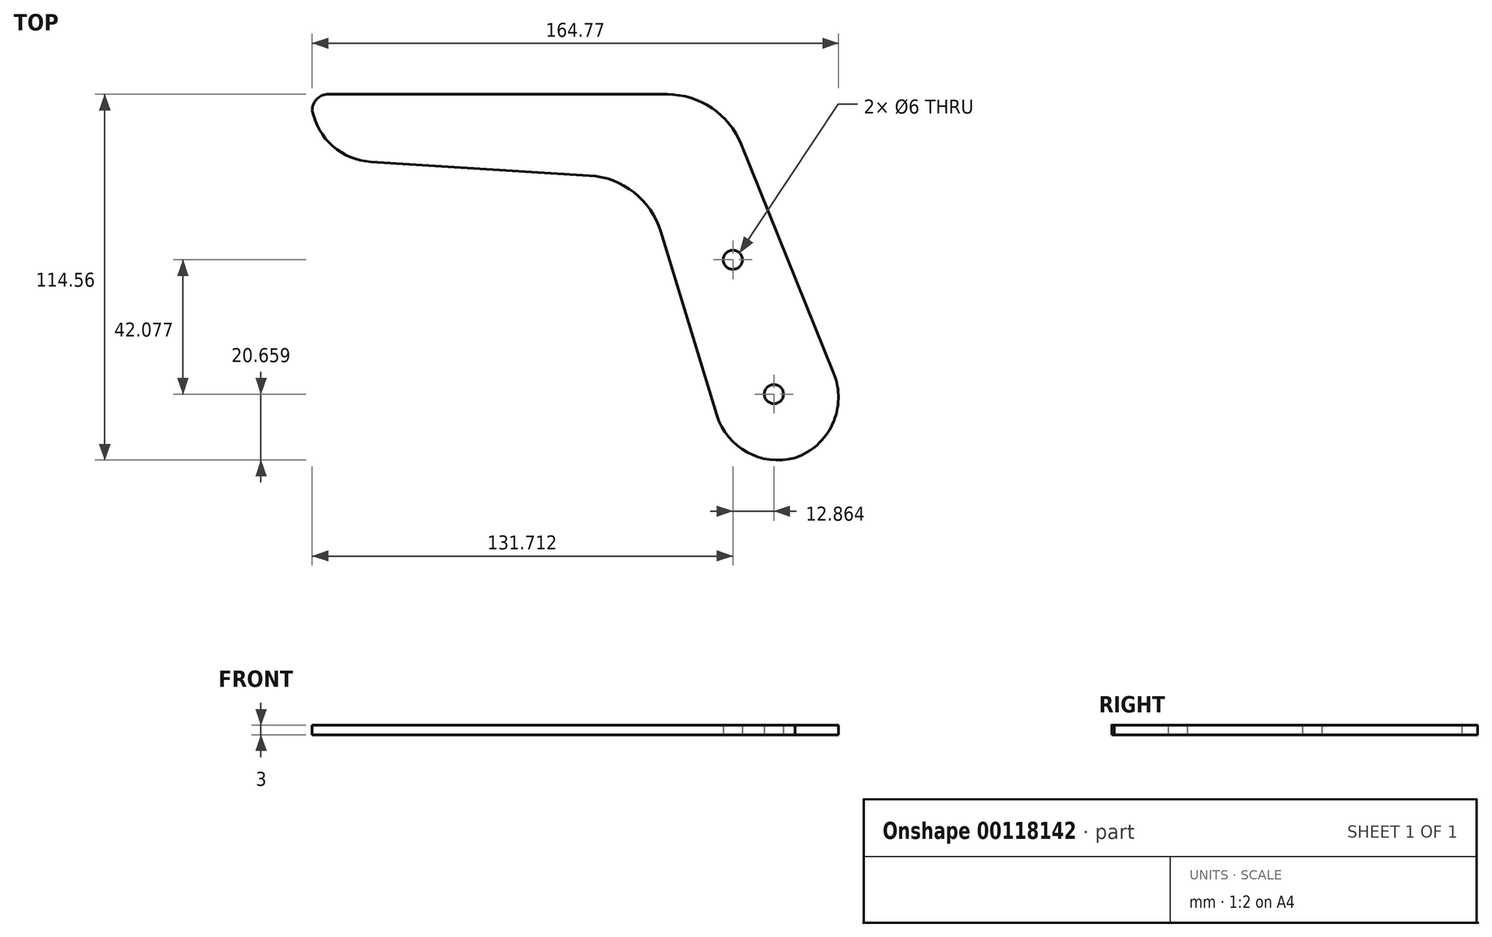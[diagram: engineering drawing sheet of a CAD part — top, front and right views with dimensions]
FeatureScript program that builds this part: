
annotation { "Feature Type Name" : "Feature", "Feature Type Description" : "" }
export const myFeature = defineFeature(function(context is Context, id is Id, definition is map)
    precondition{}
    {
        {
            var Q0;
            Q0=qCreatedBy(makeId("Top.planeOp"),FACE);
            var sketch = newSketch(context, id + "F0", { "sketchPlane" : qUnion([Q0])});
            skLineSegment(sketch, "E0", {"start": v(0, 0) * mm, "end": v(-128, 0) * mm});
            skLineSegment(sketch, "E1", {"start": v(-128, 0) * mm, "end": v(-128, -20) * mm});
            skLineSegment(sketch, "E2", {"start": v(0, 0) * mm, "end": v(0, -28) * mm, "construction": true});
            skLineSegment(sketch, "E3", {"start": v(-128, -20) * mm, "end": v(-23.9, -26.5) * mm});
            skLineSegment(sketch, "E4", {"start": v(0, 0) * mm, "end": v(43.49, -107.63) * mm});
            skPoint(sketch, "E5", {"position": v(-32, 0) * mm});
            skLineSegment(sketch, "E6", {"start": v(-32, 0) * mm, "end": v(-23.9, -26.5) * mm, "construction": true});
            skLineSegment(sketch, "E7", {"start": v(-23.9, -26.5) * mm, "end": v(0, -28) * mm, "construction": true});
            skLineSegment(sketch, "E8", {"start": v(-23.9, -26.5) * mm, "end": v(4.55, -119.54) * mm});
            skLineSegment(sketch, "E9", {"start": v(4.55, -119.54) * mm, "end": v(43.49, -107.63) * mm});
            skLineSegment(sketch, "E10.0", {"start": v(-12.13, 0) * mm, "end": v(22.72, -113.98) * mm, "construction": true});
            skPoint(sketch, "E11", {"position": v(16.58, -93.9) * mm});
            skPoint(sketch, "E12", {"position": v(3.71, -51.82) * mm});
            skCircle(sketch, "E13", {"center": v(3.71, -51.82) * mm, "radius": 3 * mm});
            skCircle(sketch, "E14", {"center": v(16.58, -93.9) * mm, "radius": 3 * mm});
            skSolve(sketch);
        }
        {
            var Q0;
            Q0=makeQuery(id+"F0.imprint","IMPRINT",FACE,{"disambiguationData":[TD([[makeQuery(id+"F0.imprint","IMPRINT",EDGE,{"derivedFrom":sQuery(id+"F0.wireOp",EDGE,"E0")}),1.0]])]});
            extrude(context, id + "F1", {"entities" : qUnion([Q0]), "depth" : 3 * mm});
        }
        {
            var Q0;
            Q0=makeQuery(id+"F1.opExtrude","SWEPT_EDGE",EDGE,{"disambiguationData":[OSD([sQuery(id+"F0.wireOp",EDGE,"E0"),sQuery(id+"F0.wireOp",EDGE,"E1")])]});
            fillet(context, id + "F2", {"entities" : qUnion([Q0]), "radius" : 5 * mm, "tangentPropagation" : true, "allowEdgeOverflow" : false});
        }
        {
            var Q0;
            Q0=makeQuery(id+"F1.opExtrude","SWEPT_EDGE",EDGE,{"disambiguationData":[OSD([sQuery(id+"F0.wireOp",EDGE,"E8"),sQuery(id+"F0.wireOp",EDGE,"E9")])]});
            var Q1;
            Q1=makeQuery(id+"F1.opExtrude","SWEPT_EDGE",EDGE,{"disambiguationData":[OSD([sQuery(id+"F0.wireOp",EDGE,"E4"),sQuery(id+"F0.wireOp",EDGE,"E9")])]});
            fillet(context, id + "F3", {"entities" : qUnion([Q0, Q1]), "radius" : 20 * mm, "tangentPropagation" : true, "allowEdgeOverflow" : false});
        }
        {
            var Q0;
            Q0=makeQuery(id+"F1.opExtrude","SWEPT_EDGE",EDGE,{"disambiguationData":[OSD([sQuery(id+"F0.wireOp",EDGE,"E1"),sQuery(id+"F0.wireOp",EDGE,"E3")])]});
            fillet(context, id + "F4", {"entities" : qUnion([Q0]), "radius" : 20 * mm, "tangentPropagation" : true, "allowEdgeOverflow" : false});
        }
        {
            var Q0;
            Q0=makeQuery(id+"F1.opExtrude","SWEPT_EDGE",EDGE,{"disambiguationData":[OSD([sQuery(id+"F0.wireOp",EDGE,"E0"),sQuery(id+"F0.wireOp",EDGE,"E4")])]});
            var Q1;
            Q1=makeQuery(id+"F1.opExtrude","SWEPT_EDGE",EDGE,{"disambiguationData":[OSD([sQuery(id+"F0.wireOp",EDGE,"E3"),sQuery(id+"F0.wireOp",EDGE,"E8")])]});
            fillet(context, id + "F5", {"entities" : qUnion([Q0, Q1]), "radius" : 25 * mm, "tangentPropagation" : true, "allowEdgeOverflow" : false});
        }
    });
